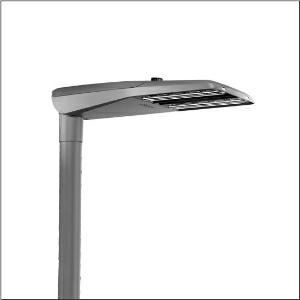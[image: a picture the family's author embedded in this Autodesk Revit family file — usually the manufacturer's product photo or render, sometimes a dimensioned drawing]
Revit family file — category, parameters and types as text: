
# Revit family: streetlight_sl_11_iq_midi___st1_2a_5xc3a41u08le_6743
name_source: partatom
category: Lighting Fixtures
units: mm (PartAtom-declared; Revit-internal decimal feet)

## family parameters
Cut with Voids When Loaded = No
Host = Face
Light Source = No
Part Type = Normal
Room Calculation Point = No
Round Connector Dimension = Use Diameter
Shared = No

## types (1)
- --- (1 x LED, 9590 lm, 59.4 W, 4000K)
    Apparent Load = 59 VA
    CIE Flux Codes = 32 70 96 100 100
    Color Rendering = 70
    Color Temperature = 4000K
    Default Elevation = 1800 mm
    Description = Streetlight SL 11 iQ midi, mast luminaire, primary light control with 3 zone facetted reflector, of plastic, silver coated, highly specular, primary optical cover: cover, of PMMA, transparent, light distribution: ST1.2a, light emission: direct distribution, primary light characteristic: asymmetric, installation type: post-top, side-entry, LED, High Power LED, rated luminous flux: 9.590lm, luminous efficacy: 161lm/W, light colour: 740, colour temperature: 4000K, control: presetting dimming logarithmic, Street-Remote, Auto-Match, Temp-Guard, Lumen-Switch, Night-Set, Smart-Wire, Light-Fading, Desk-Remote (wireless, voltage-free reading and setting of iQ features in the workshop via application-optimized NFC function/RFID function), optimised constant luminous flux control (CLO 2.0), with cable H07RN-F 5x 1.5mm², mains connection: 230..240V, AC, 50/60Hz, connection cable pre-assembled, cable length: 8,5m, start of lifetime: 59W, end of service life: 62W, reduction: 29W, luminaire housing, of diecast aluminium, powder-coated, Siteco® metallic grey (DB 702S), please order mast flange separately, inclination adjustable without tools: 0°, 5°, 10°, 15° (post-top) | 0°, -5°, -10°, -15° (side-entry), sealing non-destructively replaceable, multi-level sealing system, length: 780mm, width: 376mm, height: 118mm, mast flange for spigot size: 42mm (side-entry): 5XC10008XM4, 60/48mm (side-entry/post-top): 5XC10108XM2, 76/60mm (side-entry/post-top): 5XC10108XM1, equipment: standard, Smart Interface below, protection rating (complete): IP66, insulation class (complete): insulation class II (safety insulation), certification: CE, ENEC, VDE, UKCA, impact resistance: IK09, permissible operating ambient temperature for outdoor applications: -25..+50°C, standard-compliant lighting for roads and squares, Environmental Product Declaration (EPD) tested and certified by an independent institute, packaging unit: 1 piece

Light Distribution: ST1.2a
    Height = 118 mm
    Lamp = 1 x LED
    Lamp Light Flux = 9590 lm
    Lamp Power = 59.4 W
    Lamp count = 1
    Length = 780 mm
    Luminous efficacy = 161 lm/W
    Manufacturer = Siteco
    ModVariant = No
    Model = 5XC3A41U08LE
    Number of Poles = 1
    OnlyDefault = Yes
    Power Factor = 1
    Product Name = Streetlight SL 11 iQ midi | ST1.2a
    Product group = mast luminaire | pylon top
    ProductGroupID = 6100
    Protection Class = Protection class II
    Protection Degree = IP 66
    RLX_Detail_Level = 1
    RLX_Emergency_Light_Flux = 0 lm
    RLX_Emergency_Type = 0
    RLX_Emergency_Type_DB = No
    RlxData = <blob elided: 69749 chars, md5=82a58a6e>
    Socket = socket
    Standby Power = 0 W
    System Light Flux = 9590 lm
    System Power = 59 W
    Type Comments = factory setting: luminous flux: 100 % | dim-lin: 254 | 521 mA
    Type Image = l_1005968.jpg
    URL = http://relux.com
    VarID = @adj_064447
    Voltage = 0 V
    Weight = 0.00 kg
    Width = 376 mm

## geometry (parser evidence)
native form markers: Blend x4, Sweep x9
no freeform markers — native parametric forms only
